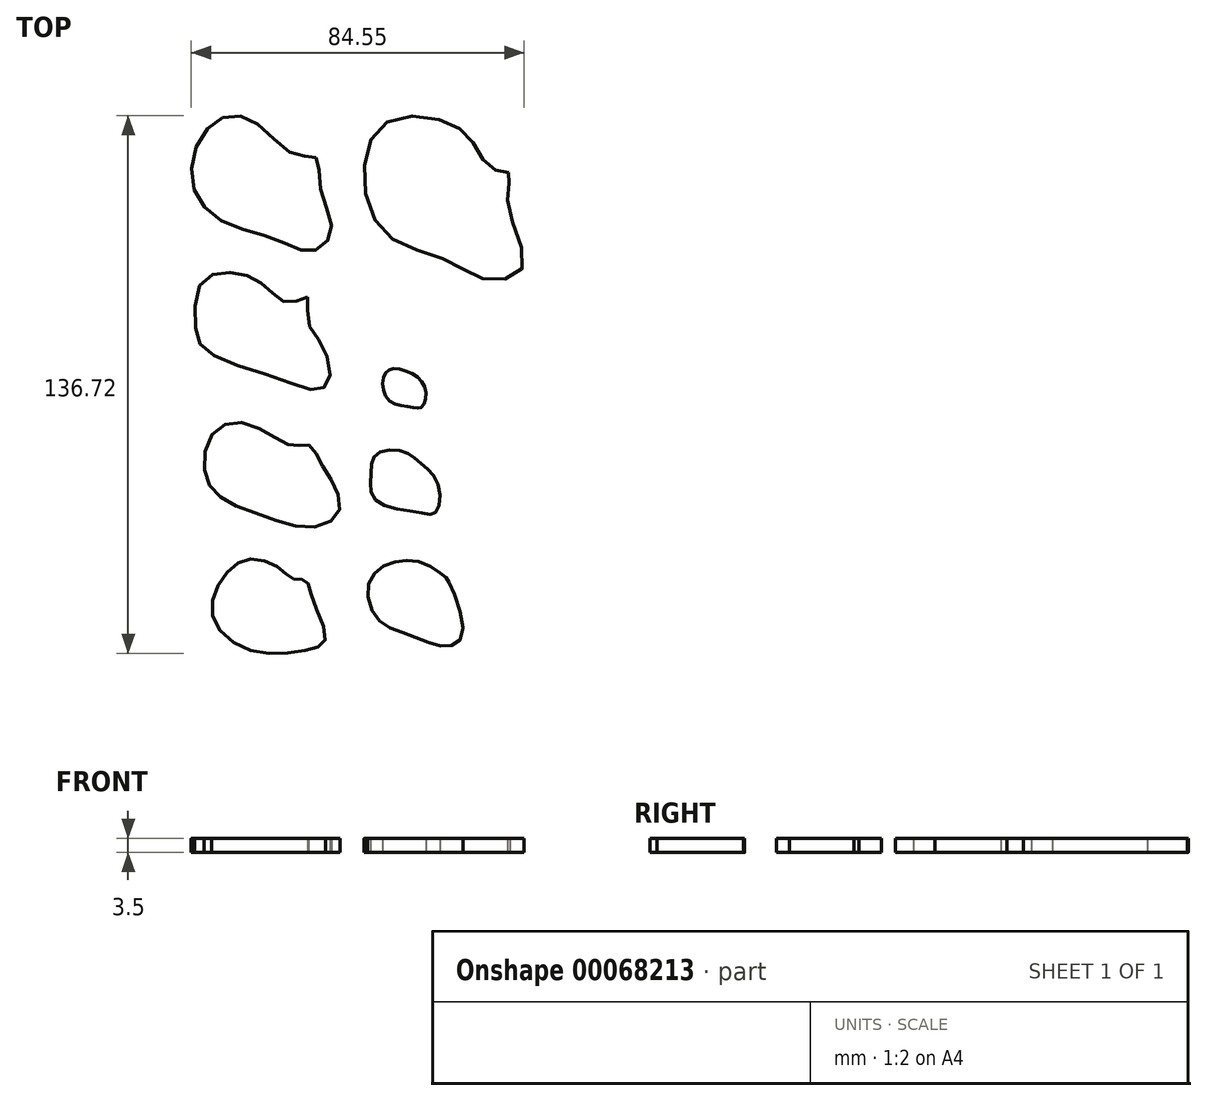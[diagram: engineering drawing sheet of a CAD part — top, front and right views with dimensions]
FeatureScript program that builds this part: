
annotation { "Feature Type Name" : "Feature", "Feature Type Description" : "" }
export const myFeature = defineFeature(function(context is Context, id is Id, definition is map)
    precondition{}
    {
        {
            var Q0;
            Q0=qCreatedBy(makeId("Top.planeOp"),FACE);
            var sketch = newSketch(context, id + "F0", { "sketchPlane" : qUnion([Q0])});
            skFitSpline(sketch, "E0", {"points": [v(-37.24, 51.53) * mm, v(-42.68, 52.3) * mm, v(-53.18, 60.86) * mm, v(-62.9, 60.67) * mm, v(-68.93, 48.03) * mm, v(-62.9, 36.56) * mm, v(-47.35, 30.72) * mm, v(-38.2, 27.8) * mm, v(-33.35, 32.86) * mm, v(-36.07, 43.56) * mm, v(-37.24, 51.53) * mm]});
            skSolve(sketch);
        }
        {
            var Q0;
            Q0=qCreatedBy(makeId("Top.planeOp"),FACE);
            var sketch = newSketch(context, id + "F1", { "sketchPlane" : qUnion([Q0])});
            skFitSpline(sketch, "E1", {"points": [v(-39.37, 16.14) * mm, v(-43.26, 14.78) * mm, v(-47.15, 16.14) * mm, v(-51.82, 20.22) * mm, v(-58.82, 22.36) * mm, v(-66.01, 20.22) * mm, v(-67.96, 8.94) * mm, v(-64.85, 2.33) * mm, v(-47.74, -4.28) * mm, v(-36.46, -7.39) * mm, v(-33.74, -4.28) * mm, v(-36.07, 4.67) * mm, v(-39.37, 10.5) * mm, v(-39.37, 16.14) * mm]});
            skSolve(sketch);
        }
        {
            var Q0;
            Q0=qCreatedBy(makeId("Top.planeOp"),FACE);
            var sketch = newSketch(context, id + "F2", { "sketchPlane" : qUnion([Q0])});
            skFitSpline(sketch, "E2", {"points": [v(-38.94, -21.47) * mm, v(-42.22, -21.67) * mm, v(-47.05, -19.93) * mm, v(-56.31, -15.68) * mm, v(-63.65, -18.77) * mm, v(-65.39, -28.62) * mm, v(-61.33, -34.8) * mm, v(-50.14, -39.62) * mm, v(-37.98, -42.32) * mm, v(-31.41, -38.46) * mm, v(-32.76, -31.32) * mm, v(-36.62, -24.95) * mm, v(-38.94, -21.47) * mm]});
            skSolve(sketch);
        }
        {
            var Q0;
            Q0=qCreatedBy(makeId("Top.planeOp"),FACE);
            var sketch = newSketch(context, id + "F3", { "sketchPlane" : qUnion([Q0])});
            skFitSpline(sketch, "E3", {"points": [v(-43, -55.45) * mm, v(-46.28, -52.94) * mm, v(-53.8, -50.43) * mm, v(-60.75, -54.87) * mm, v(-63.46, -65.1) * mm, v(-54, -73.6) * mm, v(-39.71, -73.6) * mm, v(-34.89, -70.9) * mm, v(-38.36, -59.89) * mm, v(-39.9, -55.84) * mm, v(-43, -55.45) * mm]});
            skSolve(sketch);
        }
        {
            var Q0;
            Q0=qCreatedBy(makeId("Top.planeOp"),FACE);
            var sketch = newSketch(context, id + "F4", { "sketchPlane" : qUnion([Q0])});
            skFitSpline(sketch, "E4", {"points": [v(-3.42, -56.42) * mm, v(-4.58, -54.87) * mm, v(-10.18, -51.4) * mm, v(-18.1, -51.4) * mm, v(-23.7, -56.22) * mm, v(-21.76, -65.49) * mm, v(-13.46, -69.74) * mm, v(-4.39, -72.63) * mm, v(0, -69.35) * mm, v(-3.42, -56.42) * mm]});
            skSolve(sketch);
        }
        {
            var Q0;
            Q0=qCreatedBy(makeId("Top.planeOp"),FACE);
            var sketch = newSketch(context, id + "F5", { "sketchPlane" : qUnion([Q0])});
            skFitSpline(sketch, "E5", {"points": [v(-10.56, -26.1) * mm, v(-15.2, -23.02) * mm, v(-21.95, -23.8) * mm, v(-23.3, -29) * mm, v(-22.15, -35.37) * mm, v(-10.76, -38.65) * mm, v(-6.7, -38.46) * mm, v(-6.32, -31.13) * mm, v(-10.56, -26.1) * mm]});
            skSolve(sketch);
        }
        {
            var Q0;
            Q0=qCreatedBy(makeId("Top.planeOp"),FACE);
            var sketch = newSketch(context, id + "F6", { "sketchPlane" : qUnion([Q0])});
            skFitSpline(sketch, "E6", {"points": [v(-12.88, -3.33) * mm, v(-18.28, -2.17) * mm, v(-20.22, -4.87) * mm, v(-18.48, -10.28) * mm, v(-12.88, -11.82) * mm, v(-10.37, -11.82) * mm, v(-9.4, -7.38) * mm, v(-12.88, -3.33) * mm]});
            skSolve(sketch);
        }
        {
            var Q0;
            Q0=qCreatedBy(makeId("Top.planeOp"),FACE);
            var sketch = newSketch(context, id + "F7", { "sketchPlane" : qUnion([Q0])});
            skFitSpline(sketch, "E7", {"points": [v(11.64, 47.83) * mm, v(7.4, 48.8) * mm, v(2.95, 54.97) * mm, v(-4.39, 60.76) * mm, v(-19.64, 60.38) * mm, v(-25.04, 47.06) * mm, v(-18.86, 31.61) * mm, v(-3.8, 25.44) * mm, v(6.23, 20.61) * mm, v(15.3, 23.7) * mm, v(12.02, 37.02) * mm, v(11.83, 45.13) * mm, v(11.64, 47.83) * mm]});
            skSolve(sketch);
        }
        {
            var Q0;
            Q0 = qSketchRegion(id + "F0", true);
            extrude(context, id + "F8", {"entities" : qUnion([Q0]), "depth" : 3.5 * mm});
        }
        {
            var Q0;
            Q0 = qSketchRegion(id + "F1", true);
            extrude(context, id + "F9", {"entities" : qUnion([Q0]), "depth" : 3.5 * mm});
        }
        {
            var Q0;
            Q0 = qSketchRegion(id + "F2", true);
            extrude(context, id + "F10", {"entities" : qUnion([Q0]), "depth" : 3.5 * mm});
        }
        {
            var Q0;
            Q0 = qSketchRegion(id + "F3", true);
            extrude(context, id + "F11", {"entities" : qUnion([Q0]), "depth" : 3.5 * mm});
        }
        {
            var Q0;
            Q0 = qSketchRegion(id + "F4", true);
            extrude(context, id + "F12", {"entities" : qUnion([Q0]), "depth" : 3.5 * mm});
        }
        {
            var Q0;
            Q0 = qSketchRegion(id + "F5", true);
            extrude(context, id + "F13", {"entities" : qUnion([Q0]), "depth" : 3.5 * mm});
        }
        {
            var Q0;
            Q0 = qSketchRegion(id + "F6", true);
            extrude(context, id + "F14", {"entities" : qUnion([Q0]), "depth" : 3.5 * mm});
        }
        {
            var Q0;
            Q0 = qSketchRegion(id + "F7", true);
            extrude(context, id + "F15", {"entities" : qUnion([Q0]), "depth" : 3.5 * mm});
        }
    });
